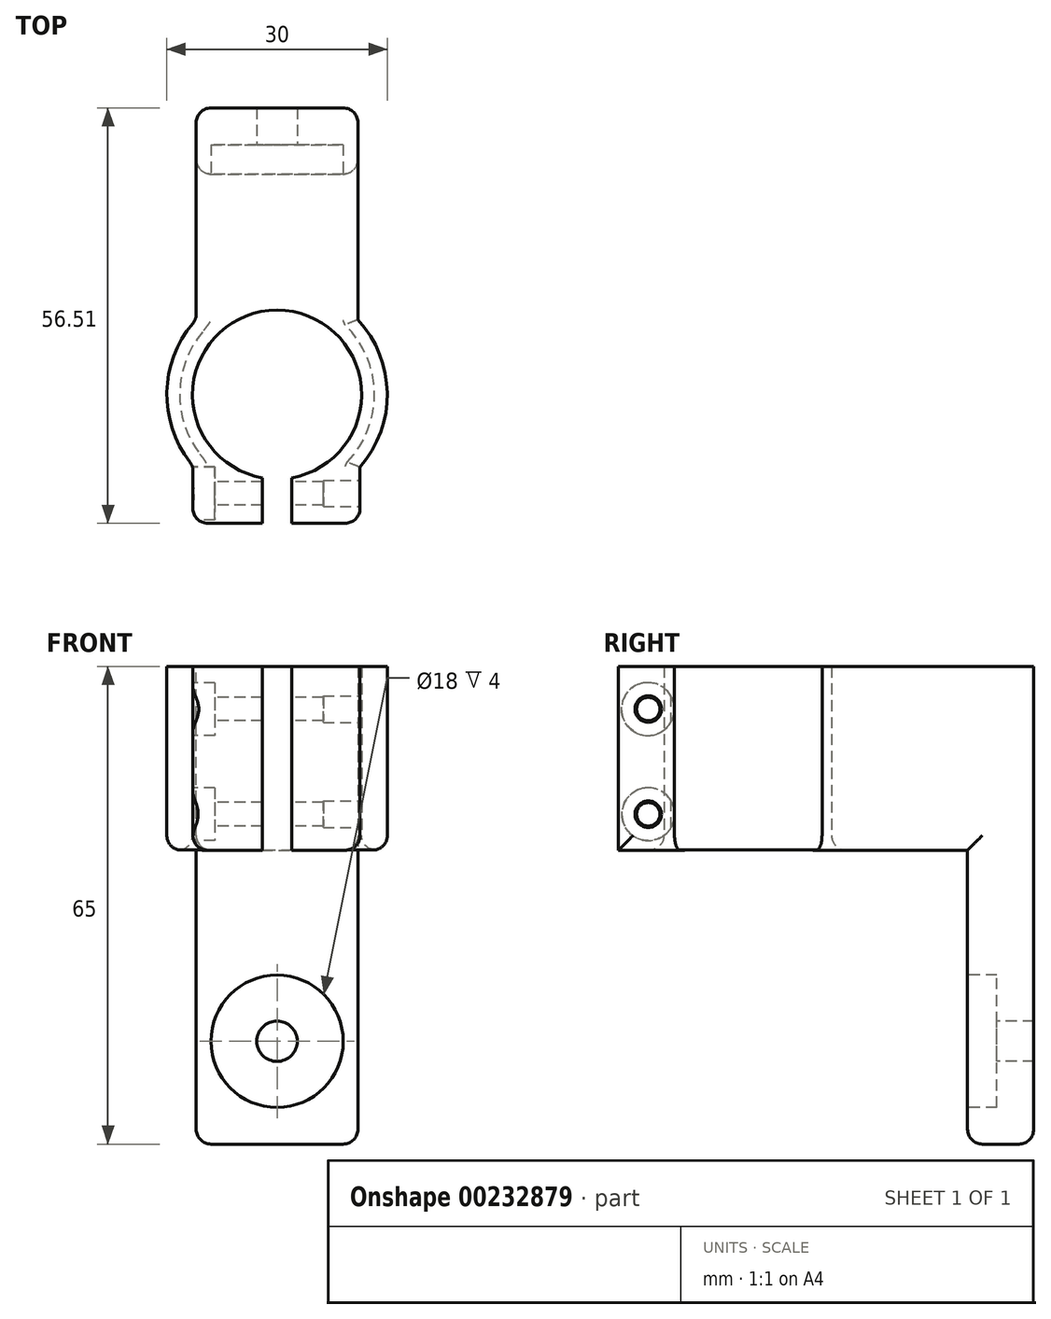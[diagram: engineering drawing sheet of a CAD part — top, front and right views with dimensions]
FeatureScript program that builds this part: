
annotation { "Feature Type Name" : "Feature", "Feature Type Description" : "" }
export const myFeature = defineFeature(function(context is Context, id is Id, definition is map)
    precondition{}
    {
        {
            var Q0;
            Q0=qCreatedBy(makeId("Top.planeOp"),FACE);
            var sketch = newSketch(context, id + "F0", { "sketchPlane" : qUnion([Q0])});
            skCircle(sketch, "E0", {"center": v(0, 0) * mm, "radius": 11.5 * mm});
            skCircle(sketch, "E1", {"center": v(0, 0) * mm, "radius": 15 * mm});
            skLineSegment(sketch, "E2.bottom", {"start": v(-11.45, -17.5) * mm, "end": v(11.29, -17.5) * mm});
            skLineSegment(sketch, "E2.top", {"start": v(-11.45, -9.5) * mm, "end": v(11.29, -9.5) * mm});
            skLineSegment(sketch, "E2.left", {"start": v(-11.45, -17.5) * mm, "end": v(-11.45, -9.5) * mm});
            skLineSegment(sketch, "E2.right", {"start": v(11.29, -17.5) * mm, "end": v(11.29, -9.5) * mm});
            skLineSegment(sketch, "E3.bottom", {"start": v(-11, 30) * mm, "end": v(11, 30) * mm});
            skLineSegment(sketch, "E3.top", {"start": v(-11, 0) * mm, "end": v(11, 0) * mm});
            skLineSegment(sketch, "E3.left", {"start": v(-11, 30) * mm, "end": v(-11, 0) * mm});
            skLineSegment(sketch, "E3.right", {"start": v(11, 30) * mm, "end": v(11, 0) * mm});
            skSolve(sketch);
        }
        {
            var Q0;
            {var subQ5=sQuery(id+"F0.wireOp",EDGE,"E2.bottom");Q0=makeQuery(id+"F0.imprint","IMPRINT",FACE,{"disambiguationData":[TD([[makeQuery(id+"F0.imprint","IMPRINT",EDGE,{"derivedFrom":subQ5}),1.0]])]});}
            var Q1;
            {var subQ5=sQuery(id+"F0.wireOp",EDGE,"E0");var subQ7=sQuery(id+"F0.wireOp",EDGE,"E3.left");var subQ9=makeQuery(id+"F0.imprint","INTERSECT",VERTEX,{"derivedFrom":[subQ5,subQ7]});Q1=makeQuery(id+"F0.imprint","IMPRINT",FACE,{"disambiguationData":[TD([[makeQuery(id+"F0.imprint","IMPRINT",EDGE,{"disambiguationData":[TD([[subQ9,-1.0]])],"derivedFrom":subQ5}),-1.0]])]});}
            var Q2;
            {var subQ1=sQuery(id+"F0.wireOp",EDGE,"E2.top");var subQ3=sQuery(id+"F0.wireOp",EDGE,"E0");var subQ7=makeQuery(id+"F0.imprint","INTERSECT",VERTEX,{"disambiguationData":[OD(0.0)],"derivedFrom":[subQ3,subQ1]});Q2=makeQuery(id+"F0.imprint","IMPRINT",FACE,{"disambiguationData":[TD([[makeQuery(id+"F0.imprint","IMPRINT",EDGE,{"disambiguationData":[TD([[subQ7,-1.0]])],"derivedFrom":subQ3}),-1.0]])]});}
            var Q3;
            {var subQ5=sQuery(id+"F0.wireOp",EDGE,"E0");var subQ7=sQuery(id+"F0.wireOp",EDGE,"E3.right");var subQ9=makeQuery(id+"F0.imprint","INTERSECT",VERTEX,{"derivedFrom":[subQ5,subQ7]});Q3=makeQuery(id+"F0.imprint","IMPRINT",FACE,{"disambiguationData":[TD([[makeQuery(id+"F0.imprint","IMPRINT",EDGE,{"disambiguationData":[TD([[subQ9,1.0]])],"derivedFrom":subQ5}),-1.0]])]});}
            var Q4;
            {var subQ0=sQuery(id+"F0.wireOp",EDGE,"E3.left");var subQ1=sQuery(id+"F0.wireOp",EDGE,"E0");var subQ2=makeQuery(id+"F0.imprint","INTERSECT",VERTEX,{"derivedFrom":[subQ1,subQ0]});Q4=makeQuery(id+"F0.imprint","IMPRINT",FACE,{"disambiguationData":[TD([[makeQuery(id+"F0.imprint","IMPRINT",EDGE,{"disambiguationData":[TD([[subQ2,1.0]])],"derivedFrom":subQ1}),-1.0]])]});}
            var Q5;
            {var subQ5=sQuery(id+"F0.wireOp",EDGE,"E3.bottom");Q5=makeQuery(id+"F0.imprint","IMPRINT",FACE,{"disambiguationData":[TD([[makeQuery(id+"F0.imprint","IMPRINT",EDGE,{"derivedFrom":subQ5}),-1.0]])]});}
            extrude(context, id + "F1", {"entities" : qUnion([Q0, Q1, Q2, Q3, Q4, Q5]), "depth" : 25 * mm});
        }
        {
            var Q0;
            Q0=makeQuery(id+"F1.opExtrude","SWEPT_FACE",FACE,{"disambiguationData":[OSD([sQuery(id+"F0.wireOp",EDGE,"E2.left")])]});
            var sketch = newSketch(context, id + "F2", { "sketchPlane" : qUnion([Q0])});
            skPoint(sketch, "E4.centerSnap0", {"position": v(13.6, 0) * mm});
            skPoint(sketch, "E5", {"position": v(13.44, 4.9) * mm});
            skCircle(sketch, "E6", {"center": v(13.44, 4.9) * mm, "radius": 3.6 * mm});
            skPoint(sketch, "E7", {"position": v(13.44, 19.2) * mm});
            skCircle(sketch, "E8", {"center": v(13.5, 19.2) * mm, "radius": 3.6 * mm});
            skSolve(sketch);
        }
        {
            var Q0;
            Q0=sQuery(id+"F2.wireOp",VERTEX,"E5");
            var Q1;
            Q1=sQuery(id+"F2.wireOp",VERTEX,"E7");
            var Q2;
            Q2=makeQuery(id+"F1.opExtrude","SWEPT_BODY",BODY,{"disambiguationData":[OSD([sQuery(id+"F0.wireOp",EDGE,"E0"),sQuery(id+"F0.wireOp",EDGE,"E1"),sQuery(id+"F0.wireOp",EDGE,"E2.bottom"),sQuery(id+"F0.wireOp",EDGE,"E2.top"),sQuery(id+"F0.wireOp",EDGE,"E2.left"),sQuery(id+"F0.wireOp",EDGE,"E2.right")])]});
            hole(context, id + "F3", {"style" : HoleStyle.SIMPLE, "endStyle" : HoleEndStyle.THROUGH, "holeDiameter" : 3.2 * mm, "locations" : qUnion([Q0, Q1]), "scope" : qUnion([Q2]), "isTappedThrough" : true});
        }
        {
            var Q0;
            Q0=qCreatedBy(makeId("Right.planeOp"),FACE);
            var sketch = newSketch(context, id + "F4", { "sketchPlane" : qUnion([Q0])});
            skLineSegment(sketch, "E9.bottom", {"start": v(0, 29) * mm, "end": v(-29.16, 29) * mm});
            skLineSegment(sketch, "E9.top", {"start": v(0, -1) * mm, "end": v(-29.16, -1) * mm});
            skLineSegment(sketch, "E9.left", {"start": v(0, 29) * mm, "end": v(0, -1) * mm});
            skLineSegment(sketch, "E9.right", {"start": v(-29.16, 29) * mm, "end": v(-29.16, -1) * mm});
            skSolve(sketch);
        }
        {
            var Q0;
            Q0 = qSketchRegion(id + "F4", true);
            extrude(context, id + "F5", {"entities" : qUnion([Q0]), "operationType" : NewBodyOperationType.REMOVE, "oppositeDirection" : true, "depth" : 2 * mm, "hasSecondDirection" : true, "secondDirectionOppositeDirection" : false, "secondDirectionDepth" : 2 * mm});
        }
        {
            var Q0;
            Q0=makeQuery(id+"F1.opExtrude","SWEPT_FACE",FACE,{"disambiguationData":[OSD([sQuery(id+"F0.wireOp",EDGE,"E3.bottom")])]});
            var sketch = newSketch(context, id + "F6", { "sketchPlane" : qUnion([Q0])});
            skLineSegment(sketch, "E10.bottom", {"start": v(-11, 25) * mm, "end": v(11, 25) * mm});
            skLineSegment(sketch, "E10.top", {"start": v(-11, -40) * mm, "end": v(11, -40) * mm});
            skLineSegment(sketch, "E10.left", {"start": v(-11, 25) * mm, "end": v(-11, -40) * mm});
            skLineSegment(sketch, "E10.right", {"start": v(11, 25) * mm, "end": v(11, -40) * mm});
            skPoint(sketch, "E11", {"position": v(0, -26) * mm});
            skSolve(sketch);
        }
        {
            var Q0;
            {var subQ0=sQuery(id+"F6.wireOp",EDGE,"E10.bottom");Q0=makeQuery(id+"F6.imprint","IMPRINT",FACE,{"disambiguationData":[TD([[makeQuery(id+"F6.imprint","IMPRINT",EDGE,{"derivedFrom":subQ0}),1.0]])]});}
            var Q1;
            {var subQ0=sQuery(id+"F6.wireOp",EDGE,"E10.top");Q1=makeQuery(id+"F6.imprint","IMPRINT",FACE,{"disambiguationData":[TD([[makeQuery(id+"F6.imprint","IMPRINT",EDGE,{"derivedFrom":subQ0}),1.0]])]});}
            extrude(context, id + "F7", {"entities" : qUnion([Q0, Q1]), "operationType" : NewBodyOperationType.ADD, "depth" : 9 * mm});
        }
        {
            var Q0;
            Q0=sQuery(id+"F6.wireOp",VERTEX,"E11");
            var Q1;
            Q1=makeQuery(id+"F1.opExtrude","SWEPT_BODY",BODY,{"disambiguationData":[OSD([sQuery(id+"F0.wireOp",EDGE,"E0"),sQuery(id+"F0.wireOp",EDGE,"E1"),sQuery(id+"F0.wireOp",EDGE,"E2.bottom"),sQuery(id+"F0.wireOp",EDGE,"E2.left"),sQuery(id+"F0.wireOp",EDGE,"E2.right"),sQuery(id+"F0.wireOp",EDGE,"E3.bottom"),sQuery(id+"F0.wireOp",EDGE,"E3.left"),sQuery(id+"F0.wireOp",EDGE,"E3.right")])]});
            hole(context, id + "F8", {"style" : HoleStyle.C_BORE, "endStyle" : HoleEndStyle.THROUGH, "oppositeDirection" : true, "holeDiameter" : 5.5 * mm, "cBoreDiameter" : 18 * mm, "cBoreDepth" : 4 * mm, "locations" : qUnion([Q0]), "scope" : qUnion([Q1]), "isTappedThrough" : true});
        }
        {
            var Q0;
            Q0=makeQuery(id+"F7.opExtrude","SWEPT_FACE",FACE,{"disambiguationData":[OSD([sQuery(id+"F6.wireOp",EDGE,"E10.top")])]});
            var Q1;
            Q1=makeQuery(id+"F8.hole-0.boolean.opBoolean","COPY",EDGE,{"derivedFrom":makeQuery(id+"F8.hole-0.opRevolve","SWEPT_EDGE",EDGE,{"disambiguationData":[OSD([sQuery(id+"F8.hole-0.sketch.wireOp",EDGE,"cbore_start_line_2"),sQuery(id+"F8.hole-0.sketch.wireOp",EDGE,"cbore_start_line_3")])]})});
            var Q2;
            Q2=makeQuery(id+"F1.opExtrude","SWEPT_EDGE",EDGE,{"disambiguationData":[OSD([sQuery(id+"F0.wireOp",EDGE,"E2.bottom"),sQuery(id+"F0.wireOp",EDGE,"E2.right")])]});
            var Q3;
            Q3=makeQuery(id+"F1.opExtrude","CAP_EDGE",EDGE,{"disambiguationData":[OSD([sQuery(id+"F0.wireOp",EDGE,"E2.right")])],"isStart":true});
            var Q4;
            Q4=makeQuery(id+"F1.opExtrude","CAP_EDGE",EDGE,{"disambiguationData":[OSD([sQuery(id+"F0.wireOp",EDGE,"E0")])],"isStart":true});
            var Q5;
            Q5=makeQuery(id+"F1.opExtrude","SWEPT_EDGE",EDGE,{"disambiguationData":[OSD([sQuery(id+"F0.wireOp",EDGE,"E2.bottom"),sQuery(id+"F0.wireOp",EDGE,"E2.left")])]});
            var Q6;
            Q6=makeQuery(id+"F1.opExtrude","CAP_EDGE",EDGE,{"disambiguationData":[OSD([sQuery(id+"F0.wireOp",EDGE,"E2.left")])],"isStart":true});
            var Q7;
            Q7=makeQuery(id+"F7.opExtrude","CAP_EDGE",EDGE,{"disambiguationData":[OSD([sQuery(id+"F6.wireOp",EDGE,"E10.left")])],"isStart":false});
            var Q8;
            Q8=makeQuery(id+"F7.opExtrude","CAP_EDGE",EDGE,{"disambiguationData":[OSD([sQuery(id+"F6.wireOp",EDGE,"E10.left")])],"isStart":true});
            var Q9;
            Q9=makeQuery(id+"F1.opExtrude","CAP_EDGE",EDGE,{"disambiguationData":[OSD([sQuery(id+"F0.wireOp",EDGE,"E3.right")])],"isStart":true});
            var Q10;
            {var subQ0=sQuery(id+"F0.wireOp",EDGE,"E1");Q10=makeQuery(id+"F1.opExtrude","CAP_EDGE",EDGE,{"disambiguationData":[OSD([subQ0]),TDD([makeQuery(id+"F0.imprint","IMPRINT",EDGE,{"disambiguationData":[TD([[makeQuery(id+"F0.imprint","INTERSECT",VERTEX,{"derivedFrom":[subQ0,sQuery(id+"F0.wireOp",EDGE,"E3.right")]}),1.0]])],"derivedFrom":subQ0})])],"isStart":true});}
            var Q11;
            Q11=makeQuery(id+"F1.opExtrude","CAP_EDGE",EDGE,{"disambiguationData":[OSD([sQuery(id+"F0.wireOp",EDGE,"E3.left")])],"isStart":true});
            var Q12;
            Q12=makeQuery(id+"F7.opExtrude","CAP_EDGE",EDGE,{"disambiguationData":[OSD([sQuery(id+"F6.wireOp",EDGE,"E10.right")])],"isStart":true});
            var Q13;
            Q13=makeQuery(id+"F7.opExtrude","CAP_EDGE",EDGE,{"disambiguationData":[OSD([sQuery(id+"F6.wireOp",EDGE,"E10.right")])],"isStart":false});
            var Q14;
            {var subQ0=sQuery(id+"F0.wireOp",EDGE,"E1");Q14=makeQuery(id+"F1.opExtrude","CAP_EDGE",EDGE,{"disambiguationData":[OSD([subQ0]),TDD([makeQuery(id+"F0.imprint","IMPRINT",EDGE,{"disambiguationData":[TD([[makeQuery(id+"F0.imprint","INTERSECT",VERTEX,{"derivedFrom":[subQ0,sQuery(id+"F0.wireOp",EDGE,"E3.left")]}),-1.0]])],"derivedFrom":subQ0})])],"isStart":true});}
            var Q15;
            Q15=makeQuery(id+"F1.opExtrude","SWEPT_EDGE",EDGE,{"disambiguationData":[OSD([sQuery(id+"F0.wireOp",EDGE,"E1"),sQuery(id+"F0.wireOp",EDGE,"E3.left")])]});
            var Q16;
            Q16=makeQuery(id+"F1.opExtrude","SWEPT_EDGE",EDGE,{"disambiguationData":[OSD([sQuery(id+"F0.wireOp",EDGE,"E1"),sQuery(id+"F0.wireOp",EDGE,"E2.left")])]});
            fillet(context, id + "F9", {"entities" : qUnion([Q0, Q1, Q2, Q3, Q4, Q5, Q6, Q7, Q8, Q9, Q10, Q11, Q12, Q13, Q14, Q15, Q16]), "radius" : 2 * mm, "tangentPropagation" : true, "allowEdgeOverflow" : false});
        }
        {
            var Q0;
            Q0=makeQuery(id+"F2.imprint","IMPRINT",FACE,{"disambiguationData":[TD([[makeQuery(id+"F2.imprint","IMPRINT",EDGE,{"derivedFrom":sQuery(id+"F2.wireOp",EDGE,"E6")}),1.0]])]});
            var Q1;
            Q1=makeQuery(id+"F2.imprint","IMPRINT",FACE,{"disambiguationData":[TD([[makeQuery(id+"F2.imprint","IMPRINT",EDGE,{"derivedFrom":sQuery(id+"F2.wireOp",EDGE,"E8")}),1.0]])]});
            var Q2;
            Q2=sQuery(id+"F2.wireOp",EDGE,"E6");
            var Q3;
            Q3=sQuery(id+"F2.wireOp",EDGE,"E8");
            extrude(context, id + "F10", {"entities" : qUnion([Q0, Q1]), "operationType" : NewBodyOperationType.REMOVE, "surfaceEntities" : qUnion([Q2, Q3]), "oppositeDirection" : true, "depth" : 3 * mm});
        }
        {
            var Q0;
            Q0=makeQuery(id+"F1.opExtrude","SWEPT_FACE",FACE,{"disambiguationData":[OSD([sQuery(id+"F0.wireOp",EDGE,"E2.right")])]});
            var sketch = newSketch(context, id + "F11", { "sketchPlane" : qUnion([Q0])});
            skCircle(sketch, "E12", {"center": v(-13.44, 19.2) * mm, "radius": 1.8 * mm});
            skCircle(sketch, "E13", {"center": v(-13.44, 4.9) * mm, "radius": 1.8 * mm});
            skSolve(sketch);
        }
        {
            var Q0;
            Q0=makeQuery(id+"F11.imprint","IMPRINT",FACE,{"disambiguationData":[TD([[makeQuery(id+"F11.imprint","IMPRINT",EDGE,{"derivedFrom":sQuery(id+"F11.wireOp",EDGE,"E12")}),1.0]])]});
            var Q1;
            Q1=makeQuery(id+"F11.imprint","IMPRINT",FACE,{"disambiguationData":[TD([[makeQuery(id+"F11.imprint","IMPRINT",EDGE,{"derivedFrom":sQuery(id+"F11.wireOp",EDGE,"E13")}),1.0]])]});
            var Q2;
            Q2=sQuery(id+"F11.wireOp",EDGE,"E12");
            var Q3;
            Q3=sQuery(id+"F11.wireOp",EDGE,"E13");
            extrude(context, id + "F12", {"entities" : qUnion([Q0, Q1]), "operationType" : NewBodyOperationType.REMOVE, "surfaceEntities" : qUnion([Q2, Q3]), "oppositeDirection" : true, "depth" : 5 * mm});
        }
    });
